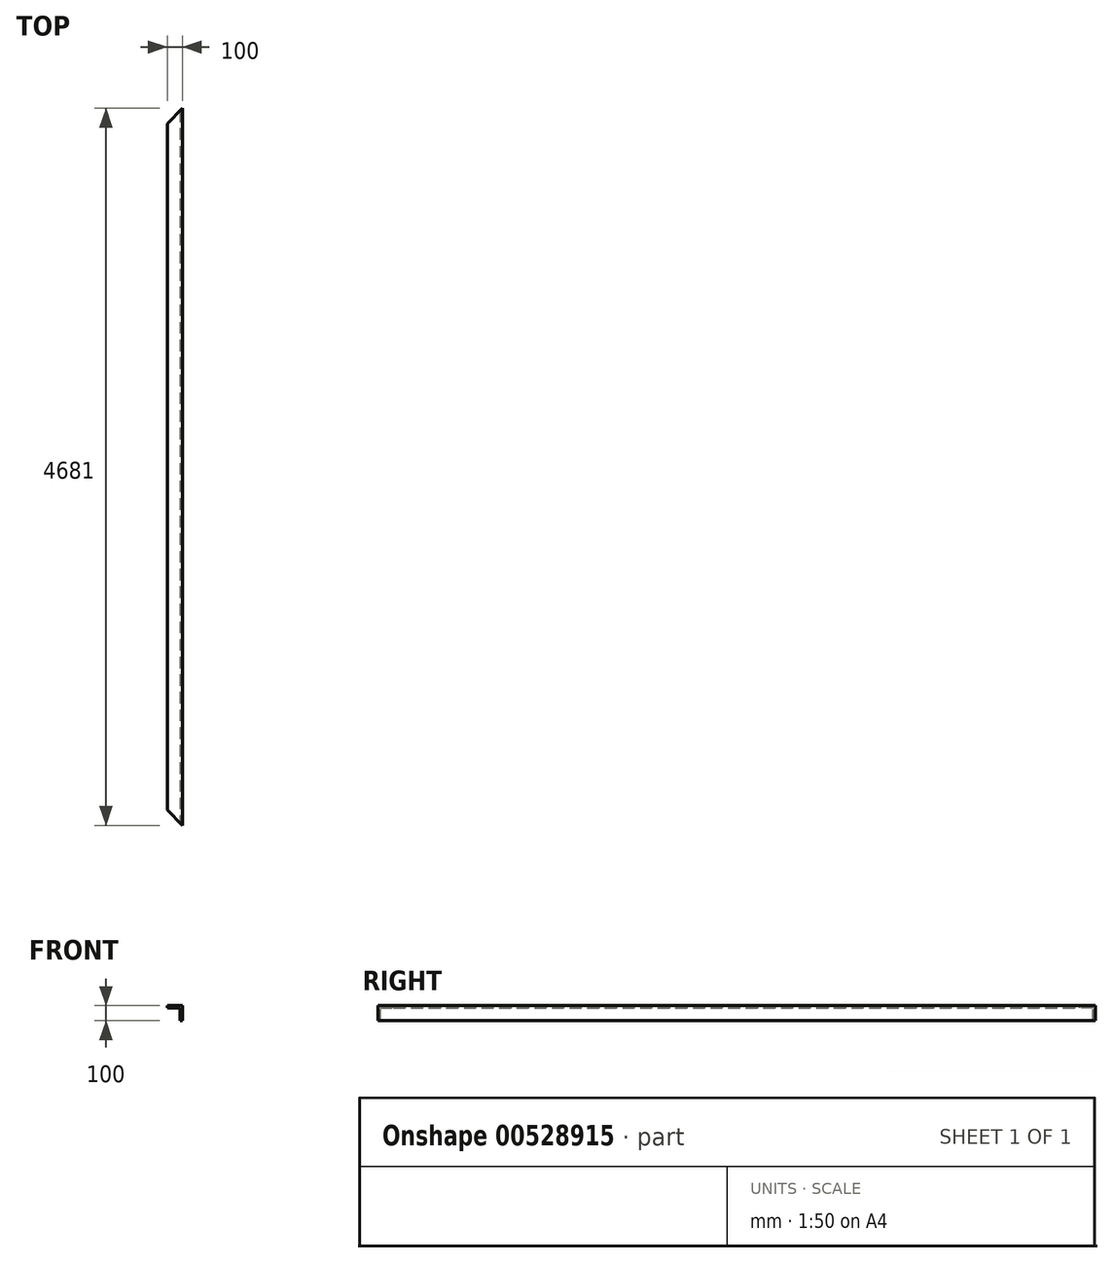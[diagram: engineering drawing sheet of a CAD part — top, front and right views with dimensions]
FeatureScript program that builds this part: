
annotation { "Feature Type Name" : "Feature", "Feature Type Description" : "" }
export const myFeature = defineFeature(function(context is Context, id is Id, definition is map)
    precondition{}
    {
        {
            var Q0;
            Q0=qCreatedBy(makeId("Top.planeOp"),FACE);
            var sketch = newSketch(context, id + "F0", { "sketchPlane" : qUnion([Q0])});
            skLineSegment(sketch, "E0", {"start": v(0, -2340.5) * mm, "end": v(0, 2340.5) * mm});
            skLineSegment(sketch, "E1", {"start": v(-100, -2240.5) * mm, "end": v(-100, 2240.5) * mm});
            skLineSegment(sketch, "E2", {"start": v(0, -2340.5) * mm, "end": v(-100, -2240.5) * mm});
            skLineSegment(sketch, "E3", {"start": v(0, 2340.5) * mm, "end": v(-100, 2240.5) * mm});
            skSolve(sketch);
        }
        {
            var Q0;
            Q0=makeQuery(id+"F0.imprint","IMPRINT",FACE,{"disambiguationData":[TD([[makeQuery(id+"F0.imprint","IMPRINT",EDGE,{"derivedFrom":sQuery(id+"F0.wireOp",EDGE,"E0")}),1.0]])]});
            extrude(context, id + "F1", {"entities" : qUnion([Q0]), "depth" : 15 * mm, "offsetDistance" : 25 * mm});
        }
        {
            var Q0;
            Q0=makeQuery(id+"F1.opExtrude","CAP_FACE",FACE,{"disambiguationData":[OSD([sQuery(id+"F0.wireOp",EDGE,"E0"),sQuery(id+"F0.wireOp",EDGE,"E1"),sQuery(id+"F0.wireOp",EDGE,"E2"),sQuery(id+"F0.wireOp",EDGE,"E3")])],"isStart":false});
            var sketch = newSketch(context, id + "F2", { "sketchPlane" : qUnion([Q0])});
            skLineSegment(sketch, "E4.0", {"start": v(0, -2340.5) * mm, "end": v(0, 2340.5) * mm});
            skLineSegment(sketch, "E5", {"start": v(-15, 2325.5) * mm, "end": v(-15, -2325.5) * mm});
            skLineSegment(sketch, "E6", {"start": v(0, 2340.5) * mm, "end": v(-15, 2325.5) * mm});
            skLineSegment(sketch, "E7", {"start": v(-15, -2325.5) * mm, "end": v(0, -2340.5) * mm});
            skSolve(sketch);
        }
        {
            var Q0;
            Q0=makeQuery(id+"F2.imprint","IMPRINT",FACE,{"disambiguationData":[TD([[makeQuery(id+"F2.imprint","IMPRINT",EDGE,{"derivedFrom":sQuery(id+"F2.wireOp",EDGE,"E4.0")}),1.0]])]});
            extrude(context, id + "F3", {"entities" : qUnion([Q0]), "operationType" : NewBodyOperationType.ADD, "depth" : (100 - 15) * mm, "offsetDistance" : 25 * mm});
        }
        {
            var Q0;
            Q0=makeQuery(id+"F1.opExtrude","SWEPT_BODY",BODY,{"disambiguationData":[OSD([sQuery(id+"F0.wireOp",EDGE,"E0"),sQuery(id+"F0.wireOp",EDGE,"E1"),sQuery(id+"F0.wireOp",EDGE,"E2"),sQuery(id+"F0.wireOp",EDGE,"E3")])]});
            var Q1;
            Q1=qCreatedBy(makeId("Top.planeOp"),FACE);
            mirror(context, id + "F4", {"entities" : qUnion([Q0]), "mirrorPlane" : qUnion([Q1])});
        }
        {
            var Q0;
            Q0=makeQuery(id+"F1.opExtrude","SWEPT_BODY",BODY,{"disambiguationData":[OSD([sQuery(id+"F0.wireOp",EDGE,"E0"),sQuery(id+"F0.wireOp",EDGE,"E1"),sQuery(id+"F0.wireOp",EDGE,"E2"),sQuery(id+"F0.wireOp",EDGE,"E3")])]});
            deleteBodies(context, id + "F5", {"entities" : qUnion([Q0])});
        }
    });
